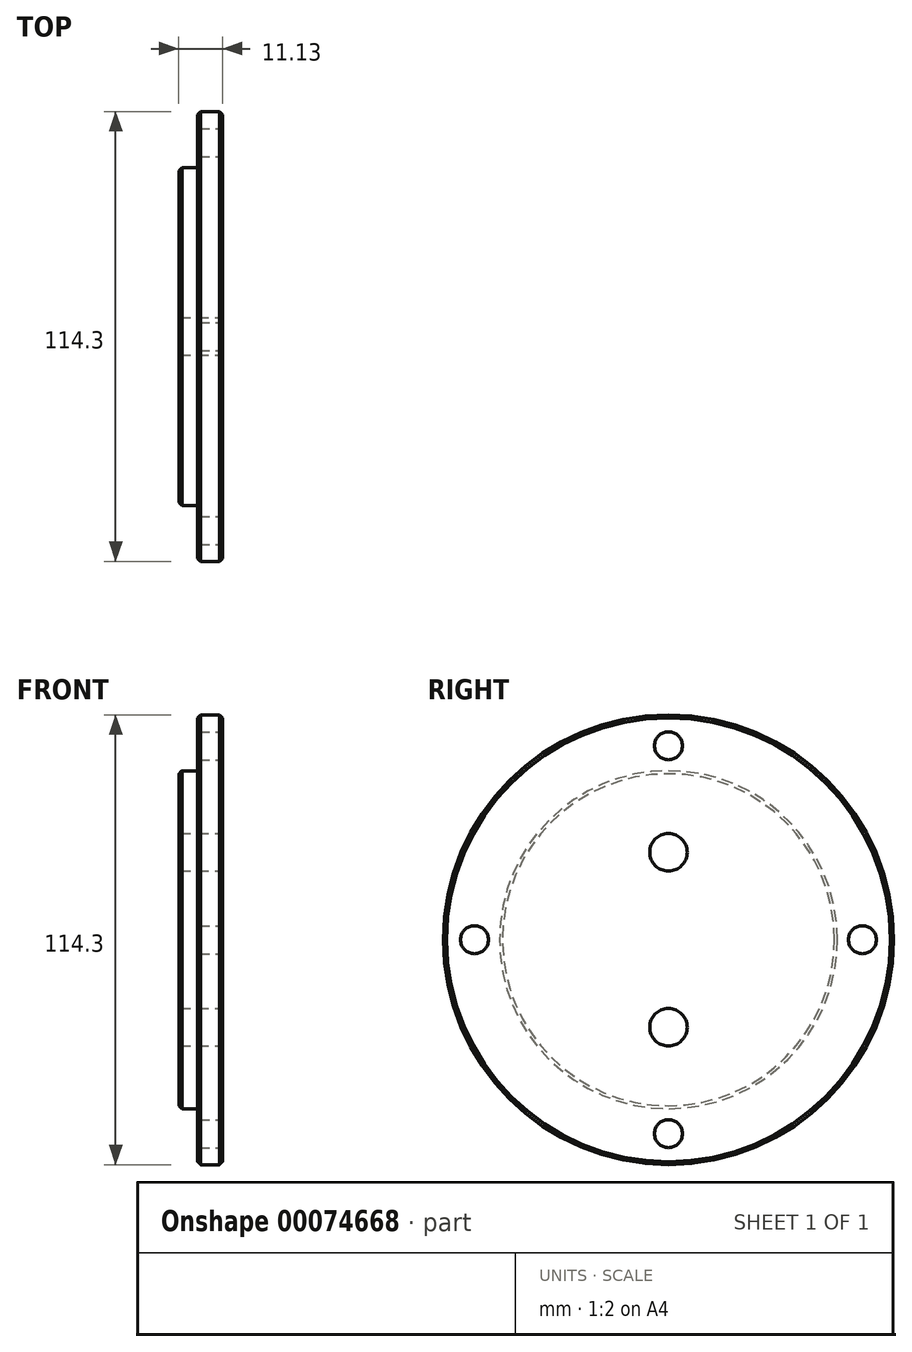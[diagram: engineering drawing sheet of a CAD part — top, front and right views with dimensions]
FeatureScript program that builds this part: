
annotation { "Feature Type Name" : "Feature", "Feature Type Description" : "" }
export const myFeature = defineFeature(function(context is Context, id is Id, definition is map)
    precondition{}
    {
        {
            var Q0;
            Q0=qCreatedBy(makeId("Right.planeOp"),FACE);
            var sketch = newSketch(context, id + "F0", { "sketchPlane" : qUnion([Q0])});
            skCircle(sketch, "E0", {"center": v(0, 0) * mm, "radius": 57.15 * mm});
            skSolve(sketch);
        }
        {
            var Q0;
            Q0 = qSketchRegion(id + "F0", true);
            extrude(context, id + "F1", {"entities" : qUnion([Q0]), "depth" : 6.35 * mm});
        }
        {
            var Q0;
            Q0=makeQuery(id+"F1.opExtrude","CAP_FACE",FACE,{"disambiguationData":[OSD([sQuery(id+"F0.wireOp",EDGE,"E0")])],"isStart":true});
            var sketch = newSketch(context, id + "F2", { "sketchPlane" : qUnion([Q0])});
            skCircle(sketch, "E1", {"center": v(0, 0) * mm, "radius": 42.93 * mm});
            skSolve(sketch);
        }
        {
            var Q0;
            Q0 = qSketchRegion(id + "F2", true);
            extrude(context, id + "F3", {"entities" : qUnion([Q0]), "operationType" : NewBodyOperationType.ADD, "depth" : 4.78 * mm});
        }
        {
            var Q0;
            Q0=makeQuery(id+"F1.opExtrude","CAP_EDGE",EDGE,{"disambiguationData":[OSD([sQuery(id+"F0.wireOp",EDGE,"E0")])],"isStart":false});
            var Q1;
            Q1=makeQuery(id+"F1.opExtrude","CAP_EDGE",EDGE,{"disambiguationData":[OSD([sQuery(id+"F0.wireOp",EDGE,"E0")])],"isStart":true});
            var Q2;
            Q2=makeQuery(id+"F3.opExtrude","CAP_EDGE",EDGE,{"disambiguationData":[OSD([sQuery(id+"F2.wireOp",EDGE,"E1")])],"isStart":false});
            chamfer(context, id + "F4", {"entities" : qUnion([Q0, Q1, Q2]), "width" : 0.76 * mm, "tangentPropagation" : true});
        }
        {
            var Q0;
            Q0=makeQuery(id+"F1.opExtrude","CAP_FACE",FACE,{"disambiguationData":[OSD([sQuery(id+"F0.wireOp",EDGE,"E0")])],"isStart":false});
            var sketch = newSketch(context, id + "F5", { "sketchPlane" : qUnion([Q0])});
            skCircle(sketch, "E2", {"center": v(0, 0) * mm, "radius": 49.28 * mm, "construction": true});
            skLineSegment(sketch, "E3", {"start": v(0, 0) * mm, "end": v(0, 77.99) * mm, "construction": true});
            skPoint(sketch, "E4", {"position": v(0, 49.28) * mm});
            skPoint(sketch, "E5.1.0", {"position": v(-49.28, 0) * mm});
            skPoint(sketch, "E5.2.0", {"position": v(0, -49.28) * mm});
            skPoint(sketch, "E5.3.0", {"position": v(49.28, 0) * mm});
            skSolve(sketch);
        }
        {
            var Q0;
            Q0=sQuery(id+"F5.wireOp",VERTEX,"E4");
            var Q1;
            Q1=sQuery(id+"F5.wireOp",VERTEX,"E5.3.0");
            var Q2;
            Q2=sQuery(id+"F5.wireOp",VERTEX,"E5.2.0");
            var Q3;
            Q3=sQuery(id+"F5.wireOp",VERTEX,"E5.1.0");
            var Q4;
            Q4=makeQuery(id+"F1.opExtrude","SWEPT_BODY",BODY,{"disambiguationData":[OSD([sQuery(id+"F0.wireOp",EDGE,"E0")])]});
            hole(context, id + "F6", {"style" : HoleStyle.SIMPLE, "holeDiameter" : 7.11 * mm, "endStyle" : HoleEndStyle.THROUGH, "locations" : qUnion([Q0, Q1, Q2, Q3]), "scope" : qUnion([Q4])});
        }
        {
            var Q0;
            Q0=makeQuery(id+"F1.opExtrude","CAP_FACE",FACE,{"disambiguationData":[OSD([sQuery(id+"F0.wireOp",EDGE,"E0")])],"isStart":false});
            var sketch = newSketch(context, id + "F7", { "sketchPlane" : qUnion([Q0])});
            skCircle(sketch, "E6", {"center": v(0, 0) * mm, "radius": 22.23 * mm, "construction": true});
            skLineSegment(sketch, "E7", {"start": v(0, 0) * mm, "end": v(0, 90.71) * mm, "construction": true});
            skPoint(sketch, "E8", {"position": v(0, 22.23) * mm});
            skPoint(sketch, "E9.1.0", {"position": v(0, -22.23) * mm});
            skSolve(sketch);
        }
        {
            var Q0;
            Q0=sQuery(id+"F7.wireOp",VERTEX,"E8");
            var Q1;
            Q1=sQuery(id+"F7.wireOp",VERTEX,"E9.1.0");
            var Q2;
            Q2=makeQuery(id+"F1.opExtrude","SWEPT_BODY",BODY,{"disambiguationData":[OSD([sQuery(id+"F0.wireOp",EDGE,"E0")])]});
            hole(context, id + "F8", {"style" : HoleStyle.SIMPLE, "holeDiameter" : 9.52 * mm, "endStyle" : HoleEndStyle.THROUGH, "locations" : qUnion([Q0, Q1]), "scope" : qUnion([Q2])});
        }
    });
